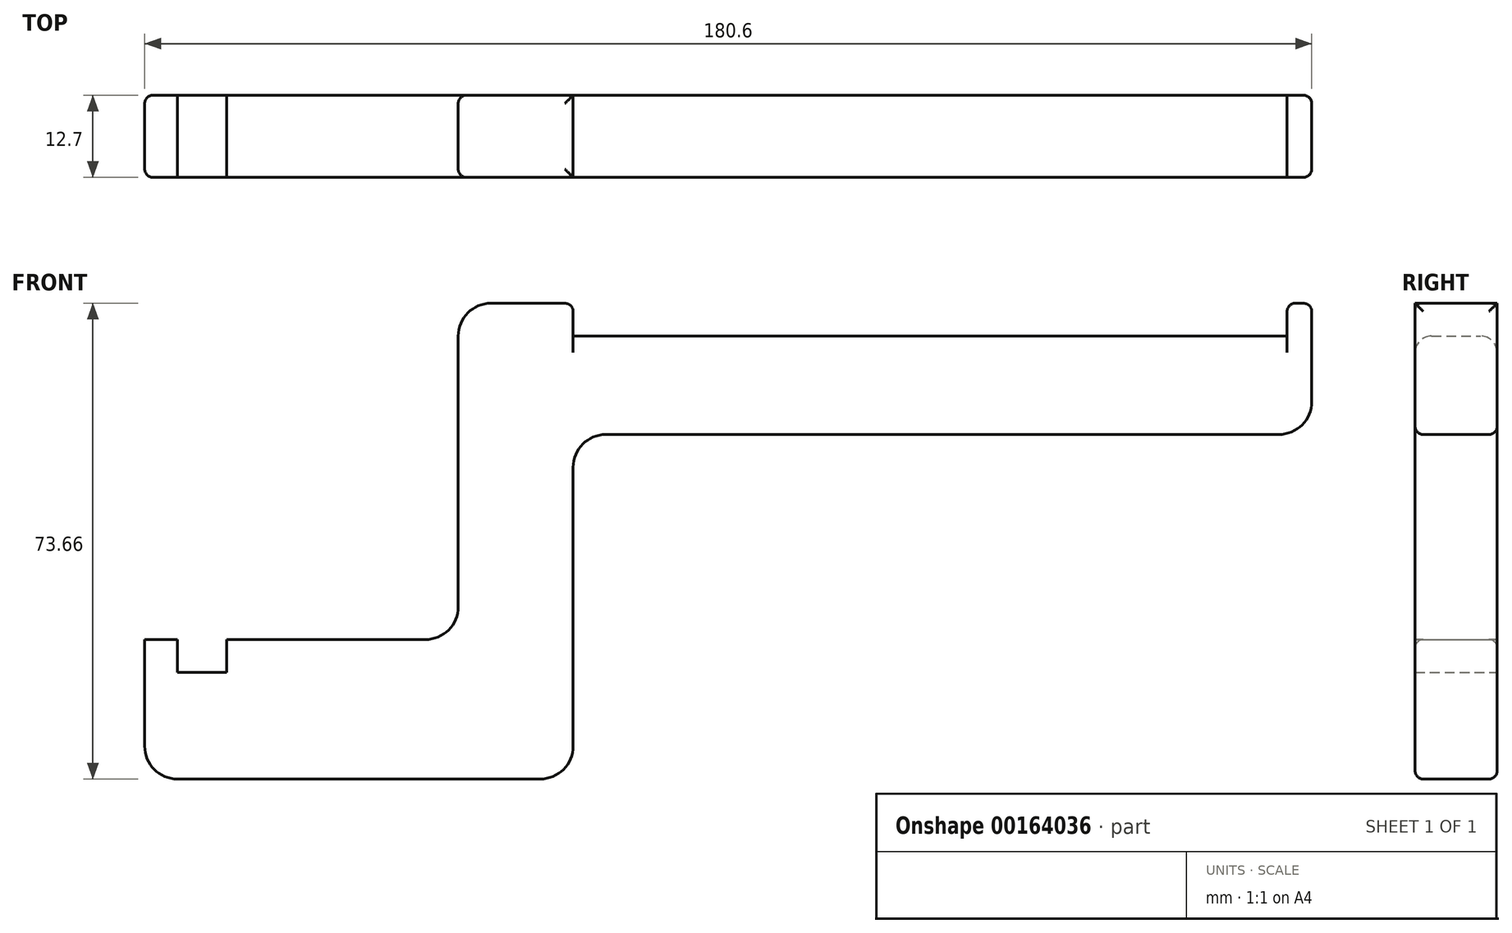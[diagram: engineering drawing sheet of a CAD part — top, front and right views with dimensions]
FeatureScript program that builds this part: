
annotation { "Feature Type Name" : "Feature", "Feature Type Description" : "" }
export const myFeature = defineFeature(function(context is Context, id is Id, definition is map)
    precondition{}
    {
        {
            var Q0;
            Q0=qCreatedBy(makeId("Front.planeOp"),FACE);
            var sketch = newSketch(context, id + "F0", { "sketchPlane" : qUnion([Q0])});
            skLineSegment(sketch, "E0", {"start": v(0, 0) * mm, "end": v(7.6, 0) * mm});
            skLineSegment(sketch, "E1", {"start": v(7.6, 0) * mm, "end": v(7.6, 5.08) * mm});
            skLineSegment(sketch, "E2", {"start": v(61.22, 5.08) * mm, "end": v(61.22, -16.51) * mm});
            skLineSegment(sketch, "E3", {"start": v(61.22, -16.51) * mm, "end": v(-5.08, -16.51) * mm});
            skLineSegment(sketch, "E4", {"start": v(-5.08, -16.51) * mm, "end": v(-5.08, 5.08) * mm});
            skLineSegment(sketch, "E5", {"start": v(-5.08, 5.08) * mm, "end": v(0, 5.08) * mm});
            skLineSegment(sketch, "E6", {"start": v(0, 5.08) * mm, "end": v(0, 0) * mm});
            skLineSegment(sketch, "E7", {"start": v(61.22, 5.08) * mm, "end": v(61.22, 36.83) * mm});
            skLineSegment(sketch, "E8", {"start": v(61.22, 36.83) * mm, "end": v(175.52, 36.83) * mm});
            skLineSegment(sketch, "E9", {"start": v(175.52, 36.83) * mm, "end": v(175.52, 57.15) * mm});
            skLineSegment(sketch, "E10", {"start": v(175.52, 57.15) * mm, "end": v(171.71, 57.15) * mm});
            skLineSegment(sketch, "E11", {"start": v(171.71, 57.15) * mm, "end": v(171.71, 52.07) * mm});
            skLineSegment(sketch, "E12", {"start": v(171.71, 52.07) * mm, "end": v(61.22, 52.07) * mm});
            skLineSegment(sketch, "E13", {"start": v(61.22, 52.07) * mm, "end": v(61.22, 57.15) * mm});
            skLineSegment(sketch, "E14", {"start": v(61.22, 57.15) * mm, "end": v(43.44, 57.15) * mm});
            skLineSegment(sketch, "E15", {"start": v(43.44, 57.15) * mm, "end": v(43.44, 5.08) * mm});
            skLineSegment(sketch, "E16", {"start": v(7.6, 5.08) * mm, "end": v(43.44, 5.08) * mm});
            skSolve(sketch);
        }
        {
            var Q0;
            Q0=makeQuery(id+"F0.imprint","IMPRINT",FACE,{"disambiguationData":[TD([[makeQuery(id+"F0.imprint","IMPRINT",EDGE,{"derivedFrom":sQuery(id+"F0.wireOp",EDGE,"E0")}),-1.0]])]});
            extrude(context, id + "F1", {"entities" : qUnion([Q0]), "depth" : 12.7 * mm});
        }
        {
            var Q0;
            Q0=makeQuery(id+"F1.opExtrude","SWEPT_EDGE",EDGE,{"disambiguationData":[OSD([sQuery(id+"F0.wireOp",EDGE,"E2"),sQuery(id+"F0.wireOp",EDGE,"E3")])]});
            var Q1;
            Q1=makeQuery(id+"F1.opExtrude","SWEPT_EDGE",EDGE,{"disambiguationData":[OSD([sQuery(id+"F0.wireOp",EDGE,"E14"),sQuery(id+"F0.wireOp",EDGE,"E15")])]});
            var Q2;
            Q2=makeQuery(id+"F1.opExtrude","SWEPT_EDGE",EDGE,{"disambiguationData":[OSD([sQuery(id+"F0.wireOp",EDGE,"E15"),sQuery(id+"F0.wireOp",EDGE,"E16")])]});
            var Q3;
            Q3=makeQuery(id+"F1.opExtrude","SWEPT_EDGE",EDGE,{"disambiguationData":[OSD([sQuery(id+"F0.wireOp",EDGE,"E7"),sQuery(id+"F0.wireOp",EDGE,"E8")])]});
            var Q4;
            Q4=makeQuery(id+"F1.opExtrude","SWEPT_EDGE",EDGE,{"disambiguationData":[OSD([sQuery(id+"F0.wireOp",EDGE,"E8"),sQuery(id+"F0.wireOp",EDGE,"E9")])]});
            var Q5;
            Q5=makeQuery(id+"F1.opExtrude","SWEPT_EDGE",EDGE,{"disambiguationData":[OSD([sQuery(id+"F0.wireOp",EDGE,"E3"),sQuery(id+"F0.wireOp",EDGE,"E4")])]});
            fillet(context, id + "F2", {"entities" : qUnion([Q0, Q1, Q2, Q3, Q4, Q5]), "radius" : 5.08 * mm, "tangentPropagation" : true, "allowEdgeOverflow" : false});
        }
        {
            var Q0;
            Q0=makeQuery(id+"F1.opExtrude","CAP_EDGE",EDGE,{"disambiguationData":[OSD([sQuery(id+"F0.wireOp",EDGE,"E12")])],"isStart":false});
            var Q1;
            Q1=makeQuery(id+"F1.opExtrude","CAP_EDGE",EDGE,{"disambiguationData":[OSD([sQuery(id+"F0.wireOp",EDGE,"E12")])],"isStart":true});
            fillet(context, id + "F3", {"entities" : qUnion([Q0, Q1]), "radius" : 2.54 * mm, "tangentPropagation" : true, "allowEdgeOverflow" : false});
        }
        {
            var Q0;
            Q0=makeQuery(id+"F1.opExtrude","CAP_EDGE",EDGE,{"disambiguationData":[OSD([sQuery(id+"F0.wireOp",EDGE,"E15")])],"isStart":false});
            var Q1;
            Q1=makeQuery(id+"F1.opExtrude","CAP_EDGE",EDGE,{"disambiguationData":[OSD([sQuery(id+"F0.wireOp",EDGE,"E16")])],"isStart":true});
            var Q2;
            Q2=makeQuery(id+"F1.opExtrude","CAP_EDGE",EDGE,{"disambiguationData":[OSD([sQuery(id+"F0.wireOp",EDGE,"E4")])],"isStart":false});
            var Q3;
            Q3=makeQuery(id+"F1.opExtrude","CAP_EDGE",EDGE,{"disambiguationData":[OSD([sQuery(id+"F0.wireOp",EDGE,"E4")])],"isStart":true});
            var Q4;
            Q4=makeQuery(id+"F1.opExtrude","SWEPT_EDGE",EDGE,{"disambiguationData":[OSD([sQuery(id+"F0.wireOp",EDGE,"E13"),sQuery(id+"F0.wireOp",EDGE,"E14")])]});
            var Q5;
            Q5=makeQuery(id+"F1.opExtrude","SWEPT_EDGE",EDGE,{"disambiguationData":[OSD([sQuery(id+"F0.wireOp",EDGE,"E10"),sQuery(id+"F0.wireOp",EDGE,"E11")])]});
            var Q6;
            Q6=makeQuery(id+"F1.opExtrude","SWEPT_EDGE",EDGE,{"disambiguationData":[OSD([sQuery(id+"F0.wireOp",EDGE,"E9"),sQuery(id+"F0.wireOp",EDGE,"E10")])]});
            fillet(context, id + "F4", {"entities" : qUnion([Q0, Q1, Q2, Q3, Q4, Q5, Q6]), "radius" : 1.27 * mm, "tangentPropagation" : true, "allowEdgeOverflow" : false});
        }
    });
